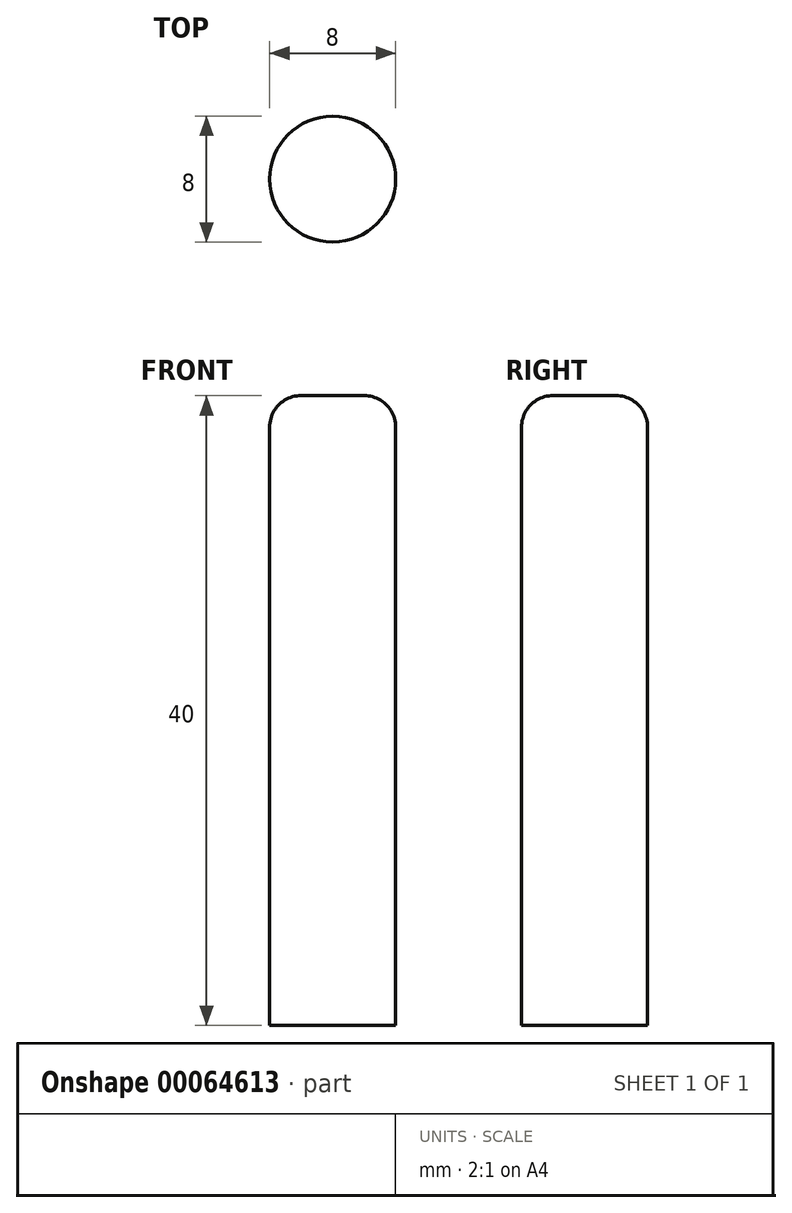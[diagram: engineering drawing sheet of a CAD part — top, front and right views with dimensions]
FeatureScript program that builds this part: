
annotation { "Feature Type Name" : "Feature", "Feature Type Description" : "" }
export const myFeature = defineFeature(function(context is Context, id is Id, definition is map)
    precondition{}
    {
        {
            var Q0;
            Q0=qCreatedBy(makeId("Top.planeOp"),FACE);
            var sketch = newSketch(context, id + "F0", { "sketchPlane" : qUnion([Q0])});
            skCircle(sketch, "E0", {"center": v(0, 0) * mm, "radius": 4 * mm});
            skSolve(sketch);
        }
        {
            var Q0;
            Q0=makeQuery(id+"F0.imprint","IMPRINT",FACE,{"disambiguationData":[TD([[makeQuery(id+"F0.imprint","IMPRINT",EDGE,{"derivedFrom":sQuery(id+"F0.wireOp",EDGE,"E0")}),1.0]])]});
            extrude(context, id + "F1", {"entities" : qUnion([Q0]), "depth" : 40 * mm});
        }
        {
            var Q0;
            Q0=makeQuery(id+"F1.opExtrude","CAP_FACE",FACE,{"disambiguationData":[OSD([sQuery(id+"F0.wireOp",EDGE,"E0")])],"isStart":false});
            fillet(context, id + "F2", {"entities" : qUnion([Q0]), "radius" : 2 * mm, "tangentPropagation" : true, "allowEdgeOverflow" : false});
        }
    });
